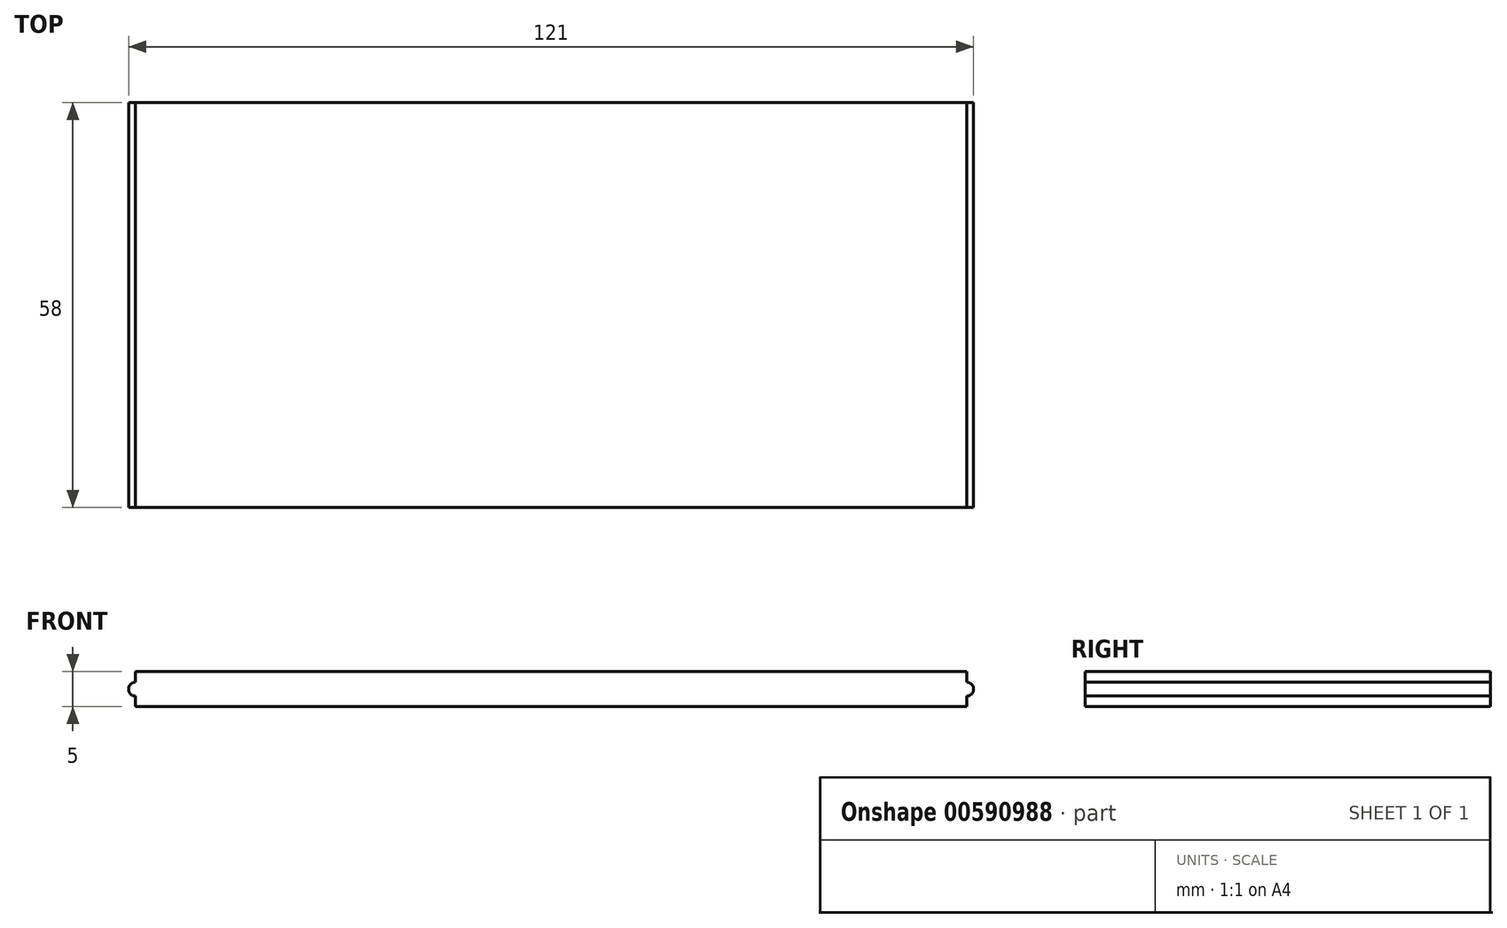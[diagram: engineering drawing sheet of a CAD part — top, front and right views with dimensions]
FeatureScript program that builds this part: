
annotation { "Feature Type Name" : "Feature", "Feature Type Description" : "" }
export const myFeature = defineFeature(function(context is Context, id is Id, definition is map)
    precondition{}
    {
        {
            var Q0;
            Q0=qCreatedBy(makeId("Top.planeOp"),FACE);
            var sketch = newSketch(context, id + "F0", { "sketchPlane" : qUnion([Q0])});
            skLineSegment(sketch, "E0.bottom", {"start": v(60.5, 29) * mm, "end": v(-60.5, 29) * mm});
            skLineSegment(sketch, "E0.top", {"start": v(60.5, -29) * mm, "end": v(-60.5, -29) * mm});
            skLineSegment(sketch, "E0.left", {"start": v(60.5, 29) * mm, "end": v(60.5, -29) * mm});
            skLineSegment(sketch, "E0.right", {"start": v(-60.5, 29) * mm, "end": v(-60.5, -29) * mm});
            skPoint(sketch, "E0.middle", {"position": v(0, 0) * mm});
            skSolve(sketch);
        }
        {
            var Q0;
            Q0=makeQuery(id+"F0.imprint","IMPRINT",FACE,{"disambiguationData":[TD([[makeQuery(id+"F0.imprint","IMPRINT",EDGE,{"derivedFrom":sQuery(id+"F0.wireOp",EDGE,"E0.bottom")}),1.0]])]});
            extrude(context, id + "F1", {"entities" : qUnion([Q0]), "depth" : 5 * mm, "offsetDistance" : 25 * mm});
        }
        {
            var Q0;
            Q0=makeQuery(id+"F1.opExtrude","SWEPT_FACE",FACE,{"disambiguationData":[OSD([sQuery(id+"F0.wireOp",EDGE,"E0.top")])]});
            var sketch = newSketch(context, id + "F2", { "sketchPlane" : qUnion([Q0])});
            skCircle(sketch, "E1", {"center": v(59.5, 2.5) * mm, "radius": 1 * mm});
            skCircle(sketch, "E2", {"center": v(-59.5, 2.5) * mm, "radius": 1 * mm});
            skLineSegment(sketch, "E3", {"start": v(-59.5, 5) * mm, "end": v(-59.5, 2.5) * mm});
            skLineSegment(sketch, "E4", {"start": v(-59.5, 2.5) * mm, "end": v(-59.5, 0) * mm});
            skLineSegment(sketch, "E5", {"start": v(59.5, 5) * mm, "end": v(59.5, 2.5) * mm});
            skLineSegment(sketch, "E6", {"start": v(59.5, 2.5) * mm, "end": v(59.5, 0) * mm});
            skSolve(sketch);
        }
        {
            var Q0;
            {var subQ0=sQuery(id+"F2.wireOp",EDGE,"E3");var subQ3=sQuery(id+"F0.wireOp",EDGE,"E0.top");var subQ6=makeQuery(id+"F1.opExtrude","CAP_EDGE",EDGE,{"disambiguationData":[OSD([subQ3])],"isStart":false});var subQ7=makeQuery(id+"F2.imprint","INTERSECT",VERTEX,{"derivedFrom":[subQ6,subQ0]});Q0=makeQuery(id+"F2.imprint","IMPRINT",FACE,{"disambiguationData":[TD([[makeQuery(id+"F2.imprint","IMPRINT",EDGE,{"disambiguationData":[TD([[subQ7,-1.0]])],"derivedFrom":subQ0}),-1.0]])]});}
            var Q1;
            {var subQ0=sQuery(id+"F2.wireOp",EDGE,"E4");var subQ3=sQuery(id+"F0.wireOp",EDGE,"E0.top");var subQ6=makeQuery(id+"F1.opExtrude","CAP_EDGE",EDGE,{"disambiguationData":[OSD([subQ3])],"isStart":true});var subQ7=makeQuery(id+"F2.imprint","INTERSECT",VERTEX,{"derivedFrom":[subQ6,subQ0]});Q1=makeQuery(id+"F2.imprint","IMPRINT",FACE,{"disambiguationData":[TD([[makeQuery(id+"F2.imprint","IMPRINT",EDGE,{"disambiguationData":[TD([[subQ7,1.0]])],"derivedFrom":subQ0}),-1.0]])]});}
            var Q2;
            {var subQ0=sQuery(id+"F2.wireOp",EDGE,"E6");var subQ3=sQuery(id+"F0.wireOp",EDGE,"E0.top");var subQ6=makeQuery(id+"F1.opExtrude","CAP_EDGE",EDGE,{"disambiguationData":[OSD([subQ3])],"isStart":true});var subQ7=makeQuery(id+"F2.imprint","INTERSECT",VERTEX,{"derivedFrom":[subQ6,subQ0]});Q2=makeQuery(id+"F2.imprint","IMPRINT",FACE,{"disambiguationData":[TD([[makeQuery(id+"F2.imprint","IMPRINT",EDGE,{"disambiguationData":[TD([[subQ7,1.0]])],"derivedFrom":subQ0}),1.0]])]});}
            var Q3;
            {var subQ0=sQuery(id+"F2.wireOp",EDGE,"E5");var subQ3=sQuery(id+"F0.wireOp",EDGE,"E0.top");var subQ6=makeQuery(id+"F1.opExtrude","CAP_EDGE",EDGE,{"disambiguationData":[OSD([subQ3])],"isStart":false});var subQ7=makeQuery(id+"F2.imprint","INTERSECT",VERTEX,{"derivedFrom":[subQ6,subQ0]});Q3=makeQuery(id+"F2.imprint","IMPRINT",FACE,{"disambiguationData":[TD([[makeQuery(id+"F2.imprint","IMPRINT",EDGE,{"disambiguationData":[TD([[subQ7,-1.0]])],"derivedFrom":subQ0}),1.0]])]});}
            extrude(context, id + "F3", {"entities" : qUnion([Q0, Q1, Q2, Q3]), "operationType" : NewBodyOperationType.REMOVE, "endBound" : BoundingType.THROUGH_ALL, "oppositeDirection" : true, "depth" : 25 * mm, "offsetDistance" : 25 * mm});
        }
    });
